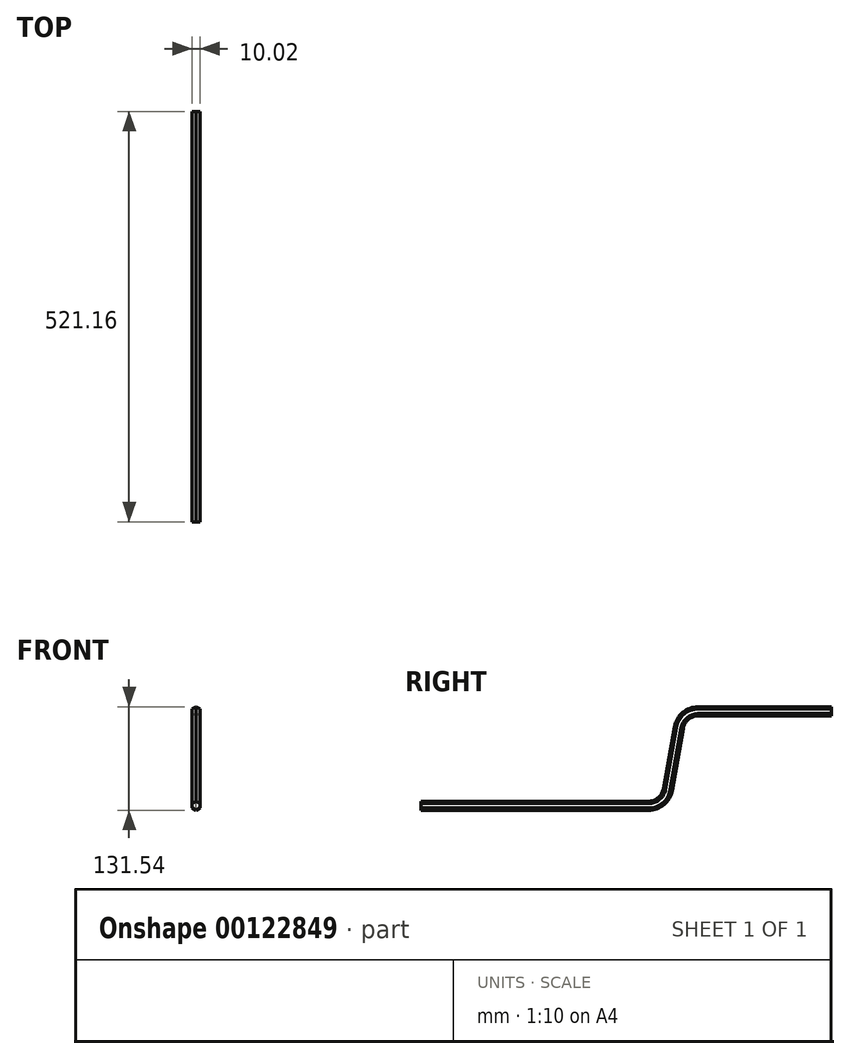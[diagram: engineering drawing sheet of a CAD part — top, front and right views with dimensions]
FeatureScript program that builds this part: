
annotation { "Feature Type Name" : "Feature", "Feature Type Description" : "" }
export const myFeature = defineFeature(function(context is Context, id is Id, definition is map)
    precondition{}
    {
        {
            var Q0;
            Q0=qCreatedBy(makeId("Front.planeOp"),FACE);
            var sketch = newSketch(context, id + "F0", { "sketchPlane" : qUnion([Q0])});
            skCircle(sketch, "E0.cCircle", {"center": v(0, 0) * mm, "radius": 5.77 * mm, "construction": true});
            skLineSegment(sketch, "E0.0", {"start": v(5, -2.88) * mm, "end": v(0.01, -5.77) * mm});
            skLineSegment(sketch, "E0.1", {"start": v(0.01, -5.77) * mm, "end": v(-5, -2.9) * mm});
            skLineSegment(sketch, "E0.2", {"start": v(-5, -2.9) * mm, "end": v(-5, 2.88) * mm});
            skLineSegment(sketch, "E0.3", {"start": v(-5, 2.88) * mm, "end": v(-0.01, 5.77) * mm});
            skLineSegment(sketch, "E0.4", {"start": v(-0.01, 5.77) * mm, "end": v(5, 2.9) * mm});
            skLineSegment(sketch, "E0.5", {"start": v(5, 2.9) * mm, "end": v(5, -2.88) * mm});
            skSolve(sketch);
        }
        {
            var Q0;
            Q0=qCreatedBy(makeId("Right.planeOp"),FACE);
            var sketch = newSketch(context, id + "F1", { "sketchPlane" : qUnion([Q0])});
            skLineSegment(sketch, "E1", {"start": v(0, 0) * mm, "end": v(289.02, 0) * mm});
            skLineSegment(sketch, "E2", {"start": v(310, 0) * mm, "end": v(440, 0) * mm, "construction": true});
            skCircle(sketch, "E3", {"center": v(440, 0) * mm, "radius": 95 * mm, "construction": true});
            skLineSegment(sketch, "E4", {"start": v(313.64, 20.66) * mm, "end": v(327.52, 99.34) * mm});
            skLineSegment(sketch, "E5", {"start": v(352.14, 120) * mm, "end": v(521.16, 120) * mm});
            skPoint(sketch, "E6.visualSharp", {"position": v(310, 0) * mm});
            skArc(sketch, "E6.filletArc", {"start": v(289.02, 0) * mm, "mid": v(305.1, 5.85) * mm, "end": v(313.64, 20.66) * mm});
            skPoint(sketch, "E7.visualSharp", {"position": v(331.16, 120) * mm});
            skArc(sketch, "E7.filletArc", {"start": v(352.14, 120) * mm, "mid": v(336.07, 114.15) * mm, "end": v(327.52, 99.34) * mm});
            skSolve(sketch);
        }
        {
            var Q0;
            Q0=makeQuery(id+"F0.imprint","IMPRINT",FACE,{"disambiguationData":[TD([[makeQuery(id+"F0.imprint","IMPRINT",EDGE,{"derivedFrom":sQuery(id+"F0.wireOp",EDGE,"E0.0")}),-1.0]])]});
            var Q1;
            Q1=sQuery(id+"F1.wireOp",EDGE,"E1");
            var Q2;
            Q2=sQuery(id+"F1.wireOp",EDGE,"E6.filletArc");
            var Q3;
            Q3=sQuery(id+"F1.wireOp",EDGE,"E4");
            var Q4;
            Q4=sQuery(id+"F1.wireOp",EDGE,"E7.filletArc");
            var Q5;
            Q5=sQuery(id+"F1.wireOp",EDGE,"E5");
            sweep(context, id + "F2", {"profiles" : qUnion([Q0]), "path" : qUnion([Q1, Q2, Q3, Q4, Q5])});
        }
    });
